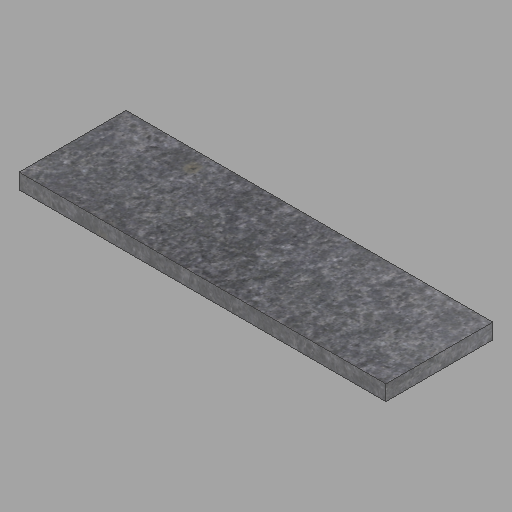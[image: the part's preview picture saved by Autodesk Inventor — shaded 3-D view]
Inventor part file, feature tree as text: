
AUTODESK INVENTOR PART (.ipt)
format: ipt  version: 2023 (Build 270158000, 158)  size: 202,752 bytes
history: native  units: in
note: dims shown in document units (in); Inventor stores cm internally (conversion verified against a paired STEP export)
features: other x1, extrude x1, sketch x1
ambient origin geometry x8: Origin, YZ Plane, XZ Plane, XY Plane, X Axis, Y Axis, Z Axis, Center Point
bodies: Solid1 (feature_tree)
feature tree (3):
  other  "2x14x48-8"
  extrude  "Extrusion1"  Depth=2.0in
  sketch  "Sketch1"  dims[d0=14.0in d1=2.0in d2=48.0in d3=0.0in]
